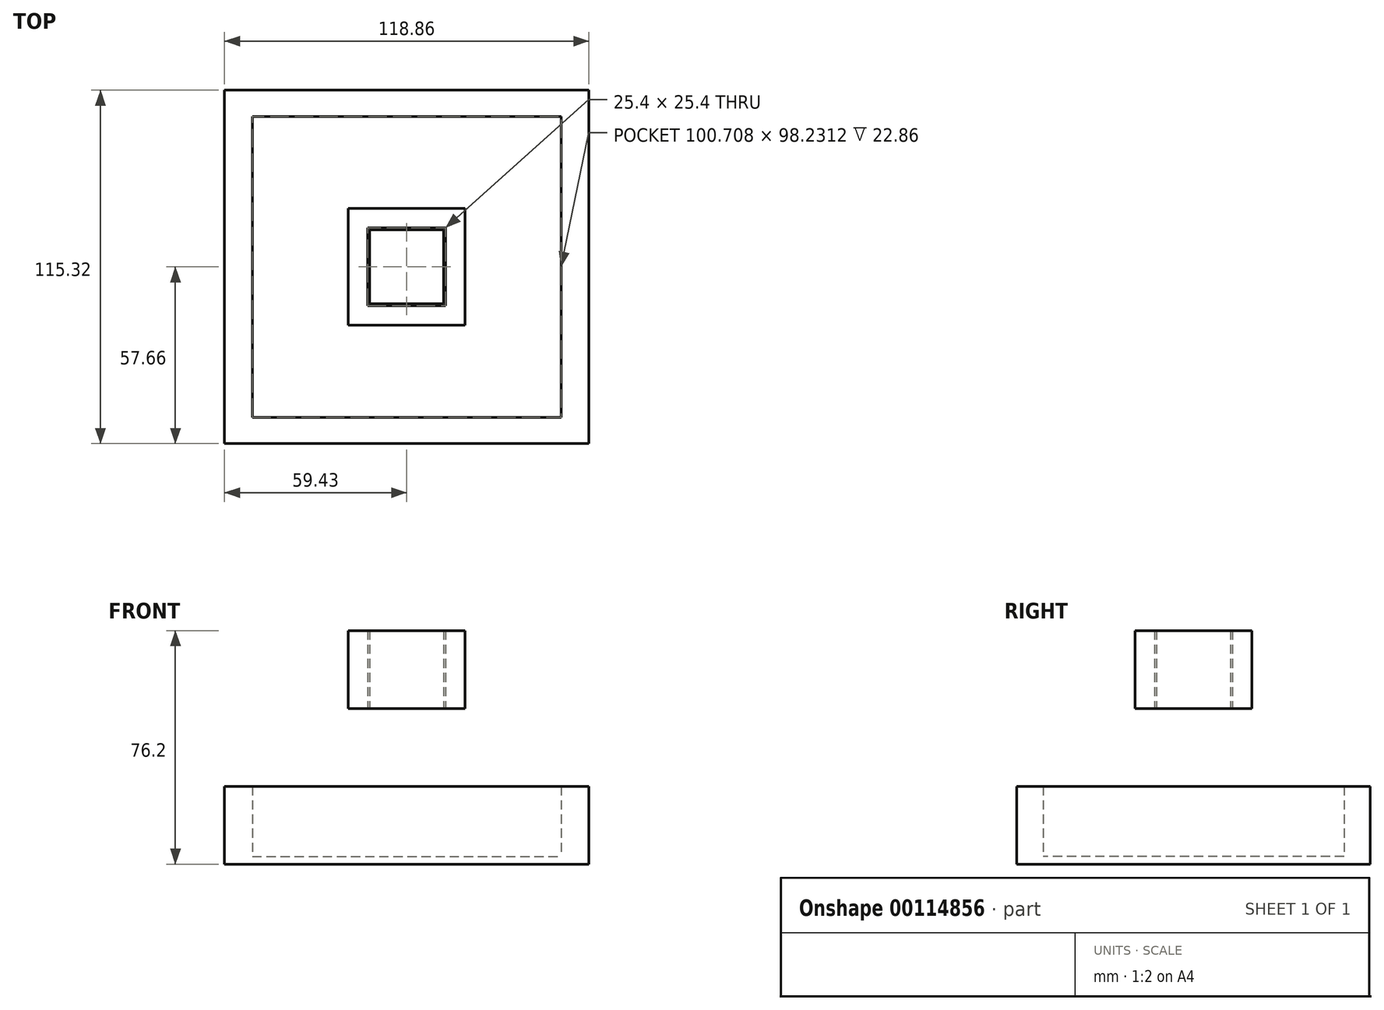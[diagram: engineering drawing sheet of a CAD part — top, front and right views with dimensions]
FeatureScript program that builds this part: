
annotation { "Feature Type Name" : "Feature", "Feature Type Description" : "" }
export const myFeature = defineFeature(function(context is Context, id is Id, definition is map)
    precondition{}
    {
        {
            var Q0;
            Q0=qCreatedBy(makeId("Top.planeOp"),FACE);
            var sketch = newSketch(context, id + "F0", { "sketchPlane" : qUnion([Q0])});
            skLineSegment(sketch, "E0.bottom", {"start": v(12.07, 12.07) * mm, "end": v(-12.06, 12.07) * mm});
            skLineSegment(sketch, "E0.top", {"start": v(12.06, -12.07) * mm, "end": v(-12.07, -12.07) * mm});
            skLineSegment(sketch, "E0.left", {"start": v(12.07, 12.06) * mm, "end": v(12.06, -12.06) * mm});
            skLineSegment(sketch, "E0.right", {"start": v(-12.07, 12.06) * mm, "end": v(-12.07, -12.06) * mm});
            skPoint(sketch, "E0.middle", {"position": v(0, 0) * mm});
            skSolve(sketch);
        }
        {
            var Q0;
            Q0=makeQuery(id+"F0.imprint","IMPRINT",FACE,{"disambiguationData":[TD([[makeQuery(id+"F0.imprint","IMPRINT",EDGE,{"derivedFrom":sQuery(id+"F0.wireOp",EDGE,"E0.bottom")}),1.0]])]});
            extrude(context, id + "F1", {"entities" : qUnion([Q0]), "depth" : 25.4 * mm});
        }
        {
            var Q0;
            Q0=qCreatedBy(makeId("Top.planeOp"),FACE);
            var sketch = newSketch(context, id + "F2", { "sketchPlane" : qUnion([Q0])});
            skLineSegment(sketch, "E1.bottom", {"start": v(19.05, 19.05) * mm, "end": v(-19.05, 19.05) * mm});
            skLineSegment(sketch, "E1.top", {"start": v(19.05, -19.05) * mm, "end": v(-19.05, -19.05) * mm});
            skLineSegment(sketch, "E1.left", {"start": v(19.05, 19.05) * mm, "end": v(19.05, -19.05) * mm});
            skLineSegment(sketch, "E1.right", {"start": v(-19.05, 19.05) * mm, "end": v(-19.05, -19.05) * mm});
            skPoint(sketch, "E1.middle", {"position": v(0, 0) * mm});
            skLineSegment(sketch, "E2.bottom", {"start": v(12.7, 12.7) * mm, "end": v(-12.7, 12.7) * mm});
            skLineSegment(sketch, "E2.top", {"start": v(12.7, -12.7) * mm, "end": v(-12.7, -12.7) * mm});
            skLineSegment(sketch, "E2.left", {"start": v(12.7, 12.7) * mm, "end": v(12.7, -12.7) * mm});
            skLineSegment(sketch, "E2.right", {"start": v(-12.7, 12.7) * mm, "end": v(-12.7, -12.7) * mm});
            skSolve(sketch);
        }
        {
            var Q0;
            Q0=makeQuery(id+"F2.imprint","IMPRINT",FACE,{"disambiguationData":[TD([[makeQuery(id+"F2.imprint","IMPRINT",EDGE,{"derivedFrom":sQuery(id+"F2.wireOp",EDGE,"E1.bottom")}),1.0]])]});
            extrude(context, id + "F3", {"entities" : qUnion([Q0]), "depth" : 25.4 * mm});
        }
        {
            var Q0;
            Q0=qCreatedBy(makeId("Top.planeOp"),FACE);
            cPlane(context, id + "F4", {"entities" : qUnion([Q0]), "cplaneType" : CPlaneType.OFFSET, "offset" : 50.8 * mm, "oppositeDirection" : true, "width" : 152.4 * mm, "height" : 152.4 * mm});
        }
        {
            var Q0;
            Q0=qCreatedBy(id+"F4.planeOp",FACE);
            var sketch = newSketch(context, id + "F5", { "sketchPlane" : qUnion([Q0])});
            skLineSegment(sketch, "E3.bottom", {"start": v(-50.35, 49.12) * mm, "end": v(50.35, 49.12) * mm});
            skLineSegment(sketch, "E3.top", {"start": v(-50.35, -49.12) * mm, "end": v(50.35, -49.12) * mm});
            skLineSegment(sketch, "E3.left", {"start": v(-50.35, 49.12) * mm, "end": v(-50.35, -49.12) * mm});
            skLineSegment(sketch, "E3.right", {"start": v(50.35, 49.12) * mm, "end": v(50.35, -49.12) * mm});
            skPoint(sketch, "E3.middle", {"position": v(0, 0) * mm});
            skLineSegment(sketch, "E4.bottom", {"start": v(-59.43, 57.66) * mm, "end": v(59.43, 57.66) * mm});
            skLineSegment(sketch, "E4.top", {"start": v(-59.43, -57.66) * mm, "end": v(59.43, -57.66) * mm});
            skLineSegment(sketch, "E4.left", {"start": v(-59.43, 57.66) * mm, "end": v(-59.43, -57.66) * mm});
            skLineSegment(sketch, "E4.right", {"start": v(59.43, 57.66) * mm, "end": v(59.43, -57.66) * mm});
            skSolve(sketch);
        }
        {
            var Q0;
            Q0=makeQuery(id+"F5.imprint","IMPRINT",FACE,{"disambiguationData":[TD([[makeQuery(id+"F5.imprint","IMPRINT",EDGE,{"derivedFrom":sQuery(id+"F5.wireOp",EDGE,"E3.bottom")}),1.0]])]});
            extrude(context, id + "F6", {"entities" : qUnion([Q0]), "depth" : 25.4 * mm});
        }
        {
            var Q0;
            Q0=makeQuery(id+"F5.imprint","IMPRINT",FACE,{"disambiguationData":[TD([[makeQuery(id+"F5.imprint","IMPRINT",EDGE,{"derivedFrom":sQuery(id+"F5.wireOp",EDGE,"E3.bottom")}),-1.0]])]});
            extrude(context, id + "F7", {"entities" : qUnion([Q0]), "operationType" : NewBodyOperationType.ADD, "depth" : 2.54 * mm});
        }
    });
